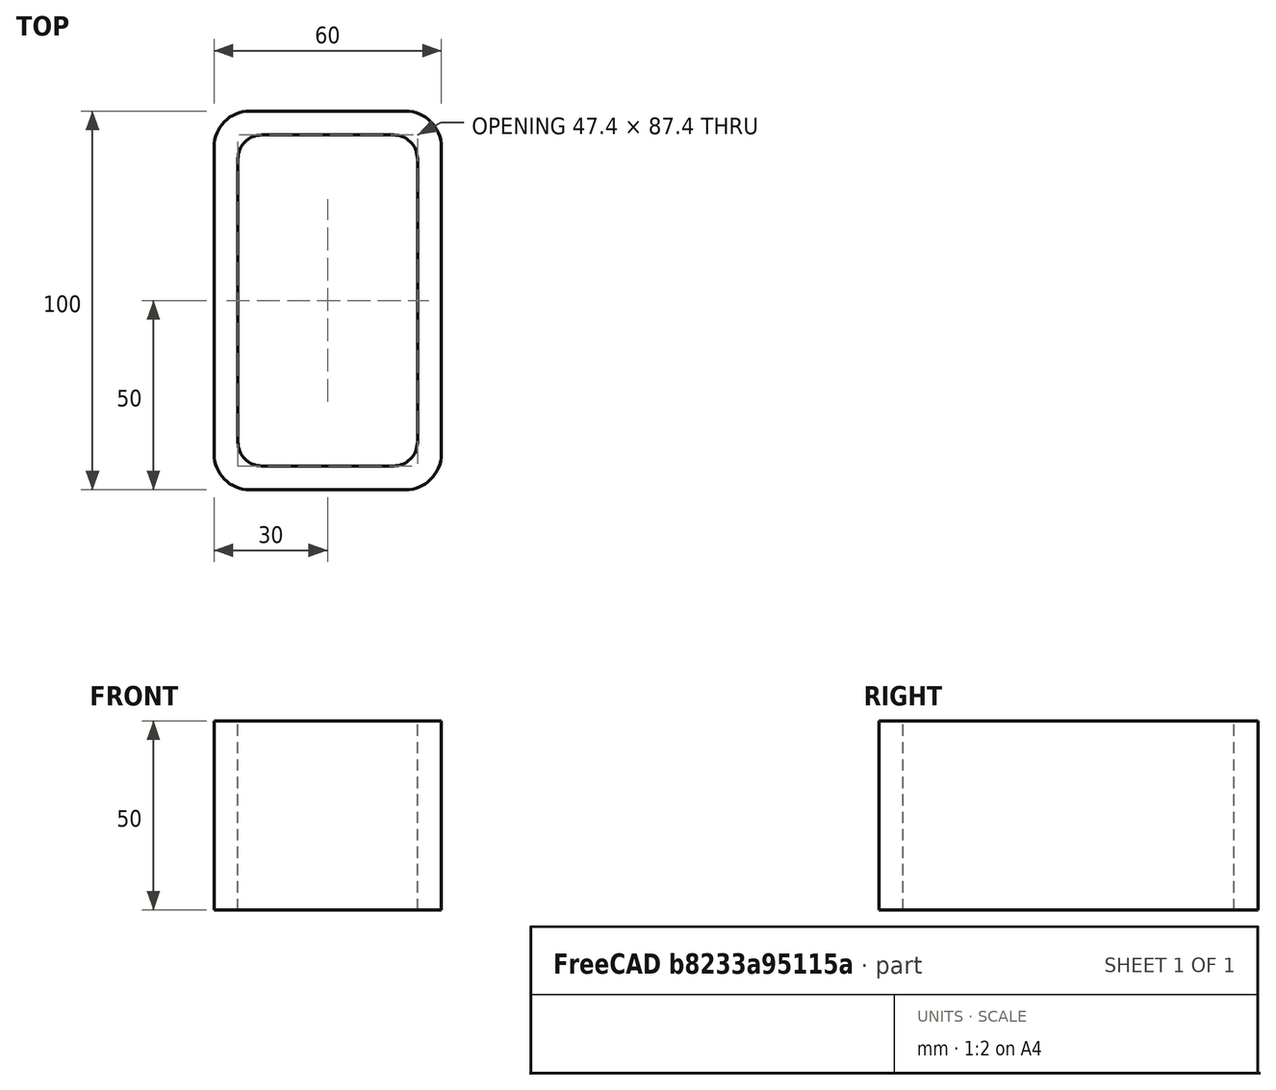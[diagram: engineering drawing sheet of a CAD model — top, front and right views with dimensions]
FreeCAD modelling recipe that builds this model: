
FCSTD DOCUMENT  (FreeCAD 0.15R4671 (Git))
Label: Rectangular hollow section 100x60x6.3 EN10219 S235JRH
License: All rights reserved
LicenseURL: http://en.wikipedia.org/wiki/All_rights_reserved
objects: Sketcher::SketchObject×1, Part::Extrusion×1
note: 2 computed .brp shape members not serialized (recipe doc carries the construction recipe); baked Part::Feature solids carry a one-line shape summary decoded from their .brp

FEATURE [Sketcher::SketchObject] Sketch
  sketch-geometry (16):
    g0: LineSegment StartX=-17.4 StartY=43.7 StartZ=0 EndX=17.4 EndY=43.7 EndZ=0
    g1: LineSegment StartX=23.7 StartY=37.4 StartZ=0 EndX=23.7 EndY=-37.4 EndZ=0
    g2: LineSegment StartX=17.4 StartY=-43.7 StartZ=0 EndX=-17.4 EndY=-43.7 EndZ=0
    g3: LineSegment StartX=-23.7 StartY=-37.4 StartZ=0 EndX=-23.7 EndY=37.4 EndZ=0
    g4: LineSegment StartX=-20.55 StartY=50 StartZ=0 EndX=20.55 EndY=50 EndZ=0
    g5: LineSegment StartX=30 StartY=40.55 StartZ=0 EndX=30 EndY=-40.55 EndZ=0
    g6: LineSegment StartX=20.55 StartY=-50 StartZ=0 EndX=-20.55 EndY=-50 EndZ=0
    g7: LineSegment StartX=-30 StartY=-40.55 StartZ=0 EndX=-30 EndY=40.55 EndZ=0
    g8: ArcOfCircle CenterX=-17.4 CenterY=37.4 CenterZ=0 NormalX=0 NormalY=0 NormalZ=1 Radius=6.3 StartAngle=1.5708 EndAngle=3.14159
    g9: ArcOfCircle CenterX=17.4 CenterY=37.4 CenterZ=0 NormalX=0 NormalY=0 NormalZ=1 Radius=6.3 StartAngle=0 EndAngle=1.5708
    g10: ArcOfCircle CenterX=17.4 CenterY=-37.4 CenterZ=0 NormalX=0 NormalY=0 NormalZ=1 Radius=6.3 StartAngle=4.71239 EndAngle=6.28319
    g11: ArcOfCircle CenterX=-17.4 CenterY=-37.4 CenterZ=0 NormalX=0 NormalY=0 NormalZ=1 Radius=6.3 StartAngle=3.14159 EndAngle=4.71239
    g12: ArcOfCircle CenterX=20.55 CenterY=40.55 CenterZ=0 NormalX=0 NormalY=0 NormalZ=1 Radius=9.45 StartAngle=0 EndAngle=1.5708
    g13: ArcOfCircle CenterX=20.55 CenterY=-40.55 CenterZ=0 NormalX=0 NormalY=0 NormalZ=1 Radius=9.45 StartAngle=4.71239 EndAngle=6.28319
    g14: ArcOfCircle CenterX=-20.55 CenterY=-40.55 CenterZ=0 NormalX=0 NormalY=0 NormalZ=1 Radius=9.45 StartAngle=3.14159 EndAngle=4.71239
    g15: ArcOfCircle CenterX=-20.55 CenterY=40.55 CenterZ=0 NormalX=0 NormalY=0 NormalZ=1 Radius=9.45 StartAngle=1.5708 EndAngle=3.14159
  constraints (36):
    c: Horizontal(g2)
    c: Vertical(g3)
    c: Horizontal(g6)
    c: Vertical(g7)
    c: Tangent(g3,g8) = 1.5708
    c: Tangent(g0,g8) = 1.5708
    c: Tangent(g0,g9) = 1.5708
    c: Tangent(g1,g9) = 1.5708
    c: Tangent(g1,g10) = 1.5708
    c: Tangent(g2,g10) = 1.5708
    c: Tangent(g2,g11) = 1.5708
    c: Tangent(g3,g11) = 1.5708
    c: Tangent(g4,g12) = 1.5708
    c: Tangent(g5,g12) = 1.5708
    c: Tangent(g5,g13) = 1.5708
    c: Tangent(g6,g13) = 1.5708
    c: Tangent(g6,g14) = 1.5708
    c: Tangent(g7,g14) = 1.5708
    c: Tangent(g7,g15) = 1.5708
    c: Tangent(g4,g15) = 1.5708
    c: Equal(g9,g8)
    c: Equal(g9,g11)
    c: Equal(g9,g10)
    c: Equal(g12,g15)
    c: Equal(g12,g14)
    c: Equal(g12,g13)
    c: Symmetric(g4,g6,g-1)
    c: Symmetric(g7,g5,g-2)
    c: DistanceY(g4,g6) = -100
    c: DistanceX(g7,g5) = 60
    c: Symmetric(g3,g1,g-2)
    c: Symmetric(g0,g2,g-1)
    c: DistanceY(g0,g4) = 6.3
    c: DistanceX(g5,g1) = -6.3
    c: Radius(g9) = 6.3
    c: Radius(g12) = 9.45
FEATURE [Part::Extrusion] Extrude  label="Rectangular hollow section 100x60x6.3 EN10219 S235JRH"
  Base = -> Sketch
  Dir = (0,0,50)
  Solid = true
